# Revit family: StopValve-(Built-in,Exposedpart)-Vitra-LiquidSeries-A42793
name_source: partatom
category: Plumbing Fixtures
revit_build: Autodesk Revit 2017 (Build: 20160225_1515(x64)
units: mm (PartAtom-declared; Revit-internal decimal feet)

## family parameters
Cut with Voids When Loaded = No
Host = Face
OmniClass Number = 23.45.00.00
OmniClass Title = Sanitary, Laundry, and Cleaning Equipment
Part Type = Normal
Room Calculation Point = No
Round Connector Dimension = Use Diameter
Shared = Yes

## types (2) — shared parameters
BIMobject category = Sanitary - Taps & Mixers
Brand = VitrA
CW Connection = Yes
Connection Diameter (mm) = 10 mm  [stored 0.0328084 ft]
Default Elevation = 850 mm  [stored 2.78871 ft]
Description = Liquid Built-In Stop valve
Design country = Turkey
HW Connection = Yes
Hot Water Supply (max.) = 80 °C
Hot Water temperature, factory set to = 38 °C
IFC Classification = Valve
Main Material = Brass
Manufacturer = Vitra
Manufacturer name = Vitra
Masterformat 2014 Code = 33 12 16
Masterformat 2014 Description = Water Utility Distribution Valves
Min. flow pressure of = 0.5 bar
Mounting type = Wall Mounted
NBS Referans Description = Valves
Nominal Depth (mm) = 70 mm
Nominal Height (mm) = 82 mm
Nominal Width (mm) = 80 mm
Number Of Connections = 1
OmniClass Code = 23-31 11 00
OmniClass Description = Faucets
Product Type = Built-in Stop Valve(exposed part)
Product certification = https://www.vitraglobal.com
Product family = Liquid
Product group = Stop Valve (exposed part)
Product url = https://www.vitraglobal.com
Range of Hot Water Supply = 5 - 65 °C
Range of flow pressure = 1 - 5 bar
Technical description = https://www.vitraglobal.com
Test Pressure = 16 bar
UNSPSC Description = Sanitary ware
URL = https://vitraglobal.com
Uniclass 1.4 Code = L7117
Uniclass 1.4 Description = Valves for water supply/distribution
Uniclass 2.0 Description = Valves
Uniclass 2015 Name = Valve products
Uniformat II Code = 22 40 00
Uniformat II Description = Plumbing Fixture
Vent Connection = No
Warranty Period (Year) = 10 Years
Waste Connection = No
Weight Net (kg) = 0.7
Youtube = https://www.youtube.com

## per-type parameters (varying)
| type | Article No. (default) | Coating Material | Color | Model | Product SKU |
| StopValve-(Built-in,Exposedpart)-Vitra-LiquidSeries-A42793 | A42793 | Chrome | Chrome | A42793 | A42793 |
| StopValve-(Built-in,Exposedpart)-Vitra-LiquidSeries-A4279339 | A4279339 | Glossy black (Metal) | Glossy black | A4279339 | A4279339 |

note: [stored X ft] marks values corroborated as IEEE doubles in the binary element streams (Revit-internal decimal feet)

## geometry (parser evidence)
native form markers: Sweep x3
no freeform markers — native parametric forms only
